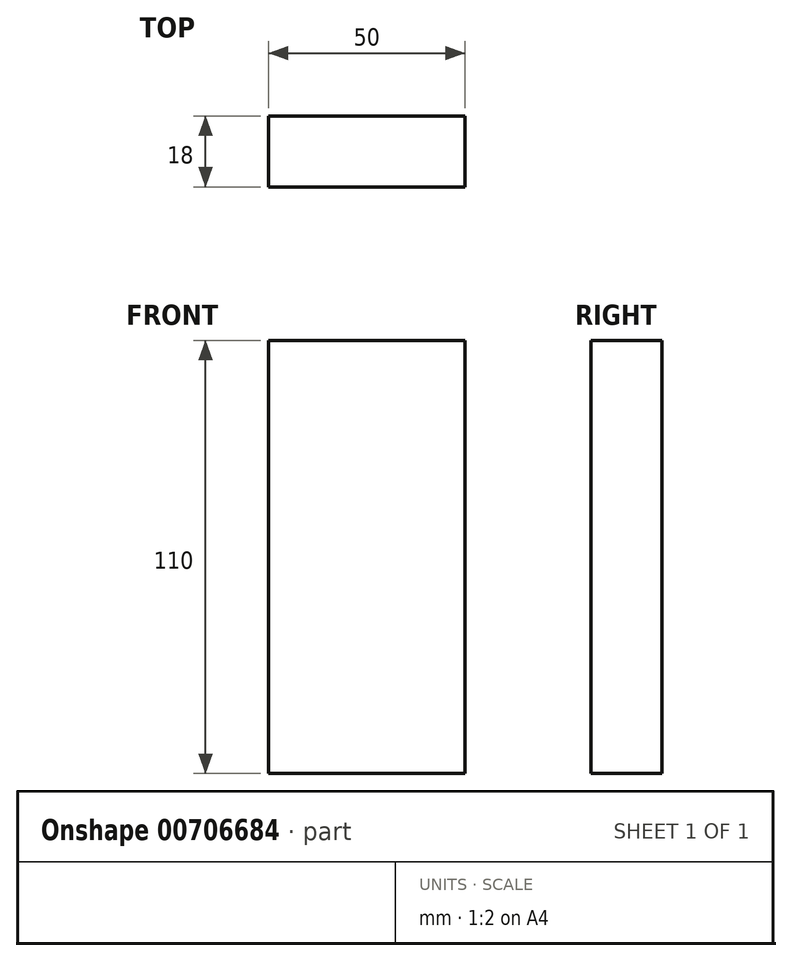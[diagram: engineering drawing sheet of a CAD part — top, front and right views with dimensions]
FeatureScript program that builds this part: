
annotation { "Feature Type Name" : "Feature", "Feature Type Description" : "" }
export const myFeature = defineFeature(function(context is Context, id is Id, definition is map)
    precondition{}
    {
        {
            var Q0;
            Q0=qCreatedBy(makeId("Front.planeOp"),FACE);
            var sketch = newSketch(context, id + "F0", { "sketchPlane" : qUnion([Q0])});
            skLineSegment(sketch, "E0.bottom", {"start": v(-25, -55) * mm, "end": v(25, -55) * mm});
            skLineSegment(sketch, "E0.top", {"start": v(-25, 55) * mm, "end": v(25, 55) * mm});
            skLineSegment(sketch, "E0.left", {"start": v(-25, -55) * mm, "end": v(-25, 55) * mm});
            skLineSegment(sketch, "E0.right", {"start": v(25, -55) * mm, "end": v(25, 55) * mm});
            skPoint(sketch, "E0.middle", {"position": v(0, 0) * mm});
            skSolve(sketch);
        }
        {
            var Q0;
            Q0=makeQuery(id+"F0.imprint","IMPRINT",FACE,{"disambiguationData":[TD([[makeQuery(id+"F0.imprint","IMPRINT",EDGE,{"derivedFrom":sQuery(id+"F0.wireOp",EDGE,"E0.bottom")}),1.0]])]});
            extrude(context, id + "F1", {"entities" : qUnion([Q0]), "depth" : 18 * mm, "offsetDistance" : 25 * mm, "symmetric" : true});
        }
    });
